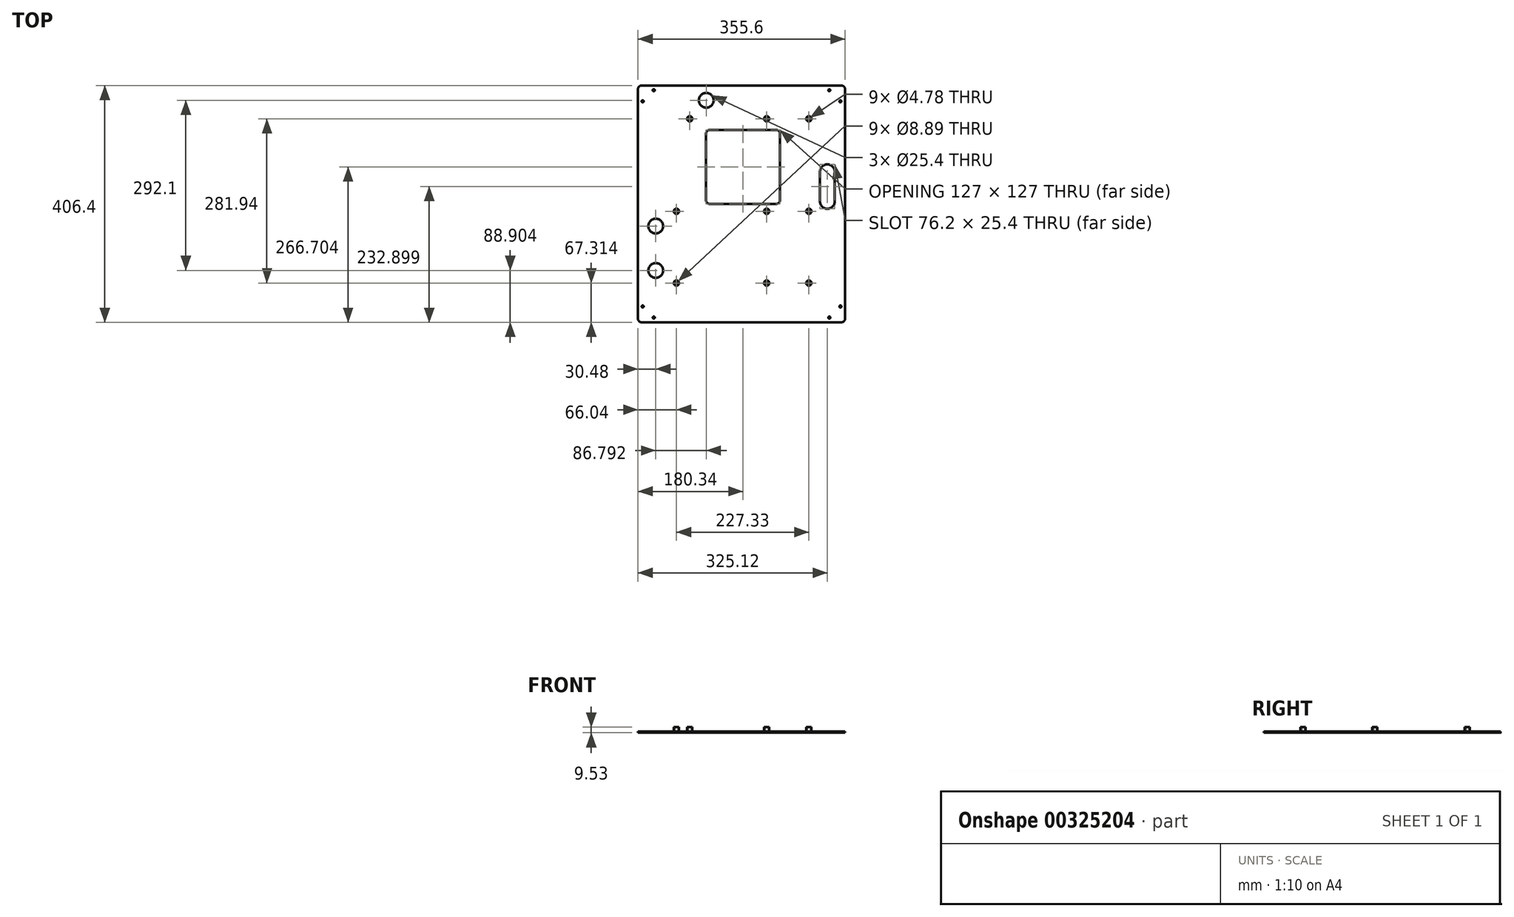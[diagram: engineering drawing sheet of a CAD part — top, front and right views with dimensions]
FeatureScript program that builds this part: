
annotation { "Feature Type Name" : "Feature", "Feature Type Description" : "" }
export const myFeature = defineFeature(function(context is Context, id is Id, definition is map)
    precondition{}
    {
        {
            var Q0;
            Q0=qCreatedBy(makeId("Top.planeOp"),FACE);
            var sketch = newSketch(context, id + "F0", { "sketchPlane" : qUnion([Q0])});
            skLineSegment(sketch, "E0.bottom", {"start": v(-150.04, 278.88) * mm, "end": v(192.86, 278.88) * mm});
            skLineSegment(sketch, "E0.top", {"start": v(-150.04, -127.52) * mm, "end": v(192.86, -127.52) * mm});
            skLineSegment(sketch, "E0.left", {"start": v(-156.4, 272.53) * mm, "end": v(-156.4, -121.17) * mm});
            skLineSegment(sketch, "E0.right", {"start": v(199.2, 272.53) * mm, "end": v(199.2, -121.17) * mm});
            skPoint(sketch, "E1", {"position": v(64.59, -76.72) * mm});
            skPoint(sketch, "E2", {"position": v(136.98, -76.72) * mm});
            skLineSegment(sketch, "E3.bottom", {"start": v(-100.51, -76.72) * mm, "end": v(143.33, -76.72) * mm});
            skLineSegment(sketch, "E3.top", {"start": v(-100.51, 228.08) * mm, "end": v(143.33, 228.08) * mm});
            skLineSegment(sketch, "E3.left", {"start": v(-100.51, -76.72) * mm, "end": v(-100.51, 228.08) * mm});
            skLineSegment(sketch, "E3.right", {"start": v(143.33, -76.72) * mm, "end": v(143.33, 228.08) * mm});
            skLineSegment(sketch, "E4", {"start": v(-100.51, 228.08) * mm, "end": v(-100.51, 140.72) * mm});
            skCircle(sketch, "E5", {"center": v(136.98, 221.73) * mm, "radius": 2.39 * mm});
            skCircle(sketch, "E6", {"center": v(64.59, 221.73) * mm, "radius": 2.39 * mm});
            skCircle(sketch, "E7", {"center": v(64.59, 221.73) * mm, "radius": 4.45 * mm});
            skCircle(sketch, "E8", {"center": v(136.98, 221.73) * mm, "radius": 4.45 * mm});
            skCircle(sketch, "E9", {"center": v(-67.5, 221.73) * mm, "radius": 2.39 * mm});
            skCircle(sketch, "E10", {"center": v(-67.5, 221.73) * mm, "radius": 4.45 * mm});
            skCircle(sketch, "E11", {"center": v(-90.35, 62.98) * mm, "radius": 2.39 * mm});
            skCircle(sketch, "E12", {"center": v(-90.35, -60.2) * mm, "radius": 2.39 * mm});
            skCircle(sketch, "E13", {"center": v(64.59, 62.98) * mm, "radius": 2.39 * mm});
            skCircle(sketch, "E14", {"center": v(64.59, -60.2) * mm, "radius": 2.39 * mm});
            skCircle(sketch, "E15", {"center": v(136.98, -60.2) * mm, "radius": 2.39 * mm});
            skCircle(sketch, "E16", {"center": v(136.98, 62.98) * mm, "radius": 2.39 * mm});
            skCircle(sketch, "E17", {"center": v(136.98, 62.98) * mm, "radius": 4.45 * mm});
            skCircle(sketch, "E18", {"center": v(64.59, 62.98) * mm, "radius": 4.45 * mm});
            skCircle(sketch, "E19", {"center": v(-90.35, 62.98) * mm, "radius": 4.45 * mm});
            skCircle(sketch, "E20", {"center": v(-90.35, -60.2) * mm, "radius": 4.45 * mm});
            skCircle(sketch, "E21", {"center": v(64.59, -60.2) * mm, "radius": 4.45 * mm});
            skCircle(sketch, "E22", {"center": v(136.98, -60.2) * mm, "radius": 4.45 * mm});
            skLineSegment(sketch, "E23", {"start": v(-100.51, -76.72) * mm, "end": v(64.59, -76.72) * mm});
            skLineSegment(sketch, "E24", {"start": v(156.03, 130.78) * mm, "end": v(156.03, 79.98) * mm});
            skLineSegment(sketch, "E25", {"start": v(181.43, 130.78) * mm, "end": v(181.43, 79.98) * mm});
            skArc(sketch, "E26", {"start": v(181.43, 130.78) * mm, "mid": v(168.73, 143.48) * mm, "end": v(156.03, 130.78) * mm});
            skArc(sketch, "E27", {"start": v(156.03, 79.98) * mm, "mid": v(168.73, 67.28) * mm, "end": v(181.43, 79.98) * mm});
            skCircle(sketch, "E28", {"center": v(-39.12, 253.48) * mm, "radius": 12.7 * mm});
            skCircle(sketch, "E29", {"center": v(-125.91, 37.58) * mm, "radius": 12.7 * mm});
            skCircle(sketch, "E30", {"center": v(-125.91, -38.62) * mm, "radius": 12.7 * mm});
            skLineSegment(sketch, "E31.bottom", {"start": v(81.1, 202.68) * mm, "end": v(-33.2, 202.68) * mm});
            skLineSegment(sketch, "E31.top", {"start": v(81.1, 75.68) * mm, "end": v(-33.2, 75.68) * mm});
            skLineSegment(sketch, "E31.left", {"start": v(87.45, 196.33) * mm, "end": v(87.45, 82.03) * mm});
            skLineSegment(sketch, "E31.right", {"start": v(-39.55, 196.33) * mm, "end": v(-39.55, 82.03) * mm});
            skPoint(sketch, "E32.visualSharp", {"position": v(87.45, 202.68) * mm});
            skArc(sketch, "E32.filletArc", {"start": v(87.45, 196.33) * mm, "mid": v(85.59, 200.82) * mm, "end": v(81.1, 202.68) * mm});
            skPoint(sketch, "E33.visualSharp", {"position": v(87.45, 75.68) * mm});
            skArc(sketch, "E33.filletArc", {"start": v(81.1, 75.68) * mm, "mid": v(85.59, 77.54) * mm, "end": v(87.45, 82.03) * mm});
            skPoint(sketch, "E34.visualSharp", {"position": v(-39.55, 75.68) * mm});
            skArc(sketch, "E34.filletArc", {"start": v(-39.55, 82.03) * mm, "mid": v(-37.7, 77.54) * mm, "end": v(-33.2, 75.68) * mm});
            skPoint(sketch, "E35.visualSharp", {"position": v(-39.55, 202.68) * mm});
            skArc(sketch, "E35.filletArc", {"start": v(-33.2, 202.68) * mm, "mid": v(-37.7, 200.82) * mm, "end": v(-39.55, 196.33) * mm});
            skPoint(sketch, "E36.visualSharp", {"position": v(-156.4, 278.88) * mm});
            skArc(sketch, "E36.filletArc", {"start": v(-150.04, 278.88) * mm, "mid": v(-154.53, 277.02) * mm, "end": v(-156.4, 272.53) * mm});
            skPoint(sketch, "E37.visualSharp", {"position": v(199.2, 278.88) * mm});
            skArc(sketch, "E37.filletArc", {"start": v(199.2, 272.53) * mm, "mid": v(197.35, 277.02) * mm, "end": v(192.86, 278.88) * mm});
            skPoint(sketch, "E38.visualSharp", {"position": v(-156.4, -127.52) * mm});
            skArc(sketch, "E38.filletArc", {"start": v(-156.4, -121.17) * mm, "mid": v(-154.53, -125.66) * mm, "end": v(-150.04, -127.52) * mm});
            skPoint(sketch, "E39.visualSharp", {"position": v(199.2, -127.52) * mm});
            skArc(sketch, "E39.filletArc", {"start": v(192.86, -127.52) * mm, "mid": v(197.35, -125.66) * mm, "end": v(199.2, -121.17) * mm});
            skCircle(sketch, "E40", {"center": v(-148.29, -100.36) * mm, "radius": 1.75 * mm});
            skCircle(sketch, "E41", {"center": v(-129.24, -119.41) * mm, "radius": 1.75 * mm});
            skCircle(sketch, "E42", {"center": v(172.06, -119.41) * mm, "radius": 1.75 * mm});
            skCircle(sketch, "E43", {"center": v(191.1, -100.36) * mm, "radius": 1.75 * mm});
            skCircle(sketch, "E44", {"center": v(-129.24, 270.78) * mm, "radius": 1.75 * mm});
            skCircle(sketch, "E45", {"center": v(-148.29, 251.73) * mm, "radius": 1.75 * mm});
            skCircle(sketch, "E46", {"center": v(172.06, 270.78) * mm, "radius": 1.75 * mm});
            skCircle(sketch, "E47", {"center": v(191.1, 251.73) * mm, "radius": 1.75 * mm});
            skSolve(sketch);
        }
        {
            var Q0;
            Q0=makeQuery(id+"F0.imprint","IMPRINT",FACE,{"disambiguationData":[TD([[makeQuery(id+"F0.imprint","IMPRINT",EDGE,{"derivedFrom":sQuery(id+"F0.wireOp",EDGE,"E3.top")}),-1.0]])]});
            var Q1;
            Q1=makeQuery(id+"F0.imprint","IMPRINT",FACE,{"disambiguationData":[TD([[makeQuery(id+"F0.imprint","IMPRINT",EDGE,{"derivedFrom":sQuery(id+"F0.wireOp",EDGE,"E13")}),1.0]])]});
            var Q2;
            {var subQ0=sQuery(id+"F0.wireOp",EDGE,"nmpgXmNF-E0IU-K8PP-zeoA-vfpKL6uIzNEA");var subQ1=makeQuery(id+"F0.imprint","IMPRINT",VERTEX,{"disambiguationData":[OD(1.0)],"derivedFrom":subQ0});Q2=makeQuery(id+"F0.imprint","IMPRINT",FACE,{"disambiguationData":[TD([[makeQuery(id+"F0.imprint","IMPRINT",EDGE,{"disambiguationData":[TD([[subQ1,1.0]])],"derivedFrom":subQ0}),-1.0]])]});}
            var Q3;
            {var subQ0=sQuery(id+"F0.wireOp",EDGE,"nmpgXmNF-E0IU-K8PP-zeoA-vfpKL6uIzNEA");var subQ1=makeQuery(id+"F0.imprint","IMPRINT",VERTEX,{"disambiguationData":[OD(1.0)],"derivedFrom":subQ0});Q3=makeQuery(id+"F0.imprint","IMPRINT",FACE,{"disambiguationData":[TD([[makeQuery(id+"F0.imprint","IMPRINT",EDGE,{"disambiguationData":[TD([[subQ1,1.0]])],"derivedFrom":subQ0}),1.0]])]});}
            var Q4;
            {var subQ0=sQuery(id+"F0.wireOp",EDGE,"nmpgXmNF-E0IU-K8PP-zeoA-vfpKL6uIzNEA");var subQ1=makeQuery(id+"F0.imprint","IMPRINT",VERTEX,{"disambiguationData":[OD(0.0)],"derivedFrom":subQ0});Q4=makeQuery(id+"F0.imprint","IMPRINT",FACE,{"disambiguationData":[TD([[makeQuery(id+"F0.imprint","IMPRINT",EDGE,{"disambiguationData":[TD([[subQ1,1.0]])],"derivedFrom":subQ0}),-1.0]])]});}
            var Q5;
            {var subQ0=sQuery(id+"F0.wireOp",EDGE,"nmpgXmNF-E0IU-K8PP-zeoA-vfpKL6uIzNEA");var subQ1=makeQuery(id+"F0.imprint","IMPRINT",VERTEX,{"disambiguationData":[OD(0.0)],"derivedFrom":subQ0});Q5=makeQuery(id+"F0.imprint","IMPRINT",FACE,{"disambiguationData":[TD([[makeQuery(id+"F0.imprint","IMPRINT",EDGE,{"disambiguationData":[TD([[subQ1,1.0]])],"derivedFrom":subQ0}),1.0]])]});}
            var Q6;
            Q6=makeQuery(id+"F0.imprint","IMPRINT",FACE,{"disambiguationData":[TD([[makeQuery(id+"F0.imprint","IMPRINT",EDGE,{"derivedFrom":sQuery(id+"F0.wireOp",EDGE,"E11")}),1.0]])]});
            var Q7;
            {var subQ7=sQuery(id+"F0.wireOp",EDGE,"E21");var subQ9=sQuery(id+"F0.wireOp",EDGE,"c2f25938-3771-4c18-96d8-fd8dbd32434b");var subQ10=makeQuery(id+"F0.imprint","INTERSECT",VERTEX,{"disambiguationData":[OD(1.0)],"derivedFrom":[subQ9,subQ7]});Q7=makeQuery(id+"F0.imprint","IMPRINT",FACE,{"disambiguationData":[TD([[makeQuery(id+"F0.imprint","IMPRINT",EDGE,{"disambiguationData":[TD([[subQ10,-1.0]])],"derivedFrom":subQ9}),-1.0]])]});}
            var Q8;
            {var subQ1=sQuery(id+"F0.wireOp",EDGE,"c2f25938-3771-4c18-96d8-fd8dbd32434b");var subQ7=sQuery(id+"F0.wireOp",EDGE,"E20");var subQ8=makeQuery(id+"F0.imprint","INTERSECT",VERTEX,{"derivedFrom":[subQ1,subQ7]});Q8=makeQuery(id+"F0.imprint","IMPRINT",FACE,{"disambiguationData":[TD([[makeQuery(id+"F0.imprint","IMPRINT",EDGE,{"disambiguationData":[TD([[subQ8,-1.0]])],"derivedFrom":subQ1}),-1.0]])]});}
            var Q9;
            {var subQ1=sQuery(id+"F0.wireOp",EDGE,"tKmp1mpe-tyhf-INWB-10SV-Ihivd2vYk6Gn.left");Q9=makeQuery(id+"F0.imprint","IMPRINT",FACE,{"disambiguationData":[TD([[makeQuery(id+"F0.imprint","IMPRINT",EDGE,{"derivedFrom":subQ1}),-1.0]])]});}
            var Q10;
            Q10=makeQuery(id+"F0.imprint","IMPRINT",FACE,{"disambiguationData":[TD([[makeQuery(id+"F0.imprint","IMPRINT",EDGE,{"derivedFrom":sQuery(id+"F0.wireOp",EDGE,"j7d80B8q-2Cgd-QsgO-YmQn-fls90DRMXYoR.bottom")}),1.0]])]});
            var Q11;
            {var subQ0=sQuery(id+"F0.wireOp",EDGE,"H0Q16ru0-qYg8-tpEI-yeED-A8eNRppSJREQ");var subQ1=sQuery(id+"F0.wireOp",EDGE,"5OOrExIu-2gan-l4Uf-qFzn-7lRf2pNMlCIK");var subQ2=makeQuery(id+"F0.imprint","INTERSECT",VERTEX,{"derivedFrom":[subQ1,subQ0]});Q11=makeQuery(id+"F0.imprint","IMPRINT",FACE,{"disambiguationData":[TD([[makeQuery(id+"F0.imprint","IMPRINT",EDGE,{"disambiguationData":[TD([[subQ2,-1.0]])],"derivedFrom":subQ1}),-1.0]])]});}
            var Q12;
            {var subQ0=sQuery(id+"F0.wireOp",EDGE,"H0Q16ru0-qYg8-tpEI-yeED-A8eNRppSJREQ");var subQ1=sQuery(id+"F0.wireOp",EDGE,"5OOrExIu-2gan-l4Uf-qFzn-7lRf2pNMlCIK");var subQ2=makeQuery(id+"F0.imprint","INTERSECT",VERTEX,{"derivedFrom":[subQ1,subQ0]});Q12=makeQuery(id+"F0.imprint","IMPRINT",FACE,{"disambiguationData":[TD([[makeQuery(id+"F0.imprint","IMPRINT",EDGE,{"disambiguationData":[TD([[subQ2,-1.0]])],"derivedFrom":subQ1}),1.0]])]});}
            var Q13;
            {var subQ0=sQuery(id+"F0.wireOp",EDGE,"f6b1ec64-6d26-4b46-bd75-5c8822b2f235");var subQ1=makeQuery(id+"F0.imprint","INTERSECT",VERTEX,{"derivedFrom":[sQuery(id+"F0.wireOp",EDGE,"c2f25938-3771-4c18-96d8-fd8dbd32434b"),subQ0]});Q13=makeQuery(id+"F0.imprint","IMPRINT",FACE,{"disambiguationData":[TD([[makeQuery(id+"F0.imprint","IMPRINT",EDGE,{"disambiguationData":[TD([[subQ1,1.0]])],"derivedFrom":subQ0}),1.0]])]});}
            var Q14;
            {var subQ0=sQuery(id+"F0.wireOp",EDGE,"f6b1ec64-6d26-4b46-bd75-5c8822b2f235");var subQ1=sQuery(id+"F0.wireOp",EDGE,"c2f25938-3771-4c18-96d8-fd8dbd32434b");var subQ2=makeQuery(id+"F0.imprint","INTERSECT",VERTEX,{"derivedFrom":[subQ1,subQ0]});Q14=makeQuery(id+"F0.imprint","IMPRINT",FACE,{"disambiguationData":[TD([[makeQuery(id+"F0.imprint","IMPRINT",EDGE,{"disambiguationData":[TD([[subQ2,1.0]])],"derivedFrom":subQ1}),1.0]])]});}
            var Q15;
            {var subQ0=sQuery(id+"F0.wireOp",EDGE,"f6b1ec64-6d26-4b46-bd75-5c8822b2f235");var subQ1=sQuery(id+"F0.wireOp",EDGE,"c2f25938-3771-4c18-96d8-fd8dbd32434b");var subQ2=makeQuery(id+"F0.imprint","INTERSECT",VERTEX,{"derivedFrom":[subQ1,subQ0]});Q15=makeQuery(id+"F0.imprint","IMPRINT",FACE,{"disambiguationData":[TD([[makeQuery(id+"F0.imprint","IMPRINT",EDGE,{"disambiguationData":[TD([[subQ2,1.0]])],"derivedFrom":subQ1}),-1.0]])]});}
            var Q16;
            {var subQ0=sQuery(id+"F0.wireOp",EDGE,"83397e81-86f9-44f2-9538-2e7c31147ec4");var subQ1=sQuery(id+"F0.wireOp",EDGE,"c2f25938-3771-4c18-96d8-fd8dbd32434b");var subQ2=makeQuery(id+"F0.imprint","INTERSECT",VERTEX,{"derivedFrom":[subQ1,subQ0]});Q16=makeQuery(id+"F0.imprint","IMPRINT",FACE,{"disambiguationData":[TD([[makeQuery(id+"F0.imprint","IMPRINT",EDGE,{"disambiguationData":[TD([[subQ2,-1.0]])],"derivedFrom":subQ1}),-1.0]])]});}
            var Q17;
            {var subQ0=sQuery(id+"F0.wireOp",EDGE,"83397e81-86f9-44f2-9538-2e7c31147ec4");var subQ1=sQuery(id+"F0.wireOp",EDGE,"c2f25938-3771-4c18-96d8-fd8dbd32434b");var subQ2=makeQuery(id+"F0.imprint","INTERSECT",VERTEX,{"derivedFrom":[subQ1,subQ0]});Q17=makeQuery(id+"F0.imprint","IMPRINT",FACE,{"disambiguationData":[TD([[makeQuery(id+"F0.imprint","IMPRINT",EDGE,{"disambiguationData":[TD([[subQ2,-1.0]])],"derivedFrom":subQ1}),1.0]])]});}
            var Q18;
            {var subQ0=sQuery(id+"F0.wireOp",EDGE,"E14");var subQ1=sQuery(id+"F0.wireOp",EDGE,"c2f25938-3771-4c18-96d8-fd8dbd32434b");var subQ2=makeQuery(id+"F0.imprint","INTERSECT",VERTEX,{"disambiguationData":[OD(0.0)],"derivedFrom":[subQ1,subQ0]});Q18=makeQuery(id+"F0.imprint","IMPRINT",FACE,{"disambiguationData":[TD([[makeQuery(id+"F0.imprint","IMPRINT",EDGE,{"disambiguationData":[TD([[subQ2,-1.0]])],"derivedFrom":subQ1}),1.0]])]});}
            var Q19;
            {var subQ0=sQuery(id+"F0.wireOp",EDGE,"E14");var subQ1=sQuery(id+"F0.wireOp",EDGE,"c2f25938-3771-4c18-96d8-fd8dbd32434b");var subQ2=makeQuery(id+"F0.imprint","INTERSECT",VERTEX,{"disambiguationData":[OD(0.0)],"derivedFrom":[subQ1,subQ0]});Q19=makeQuery(id+"F0.imprint","IMPRINT",FACE,{"disambiguationData":[TD([[makeQuery(id+"F0.imprint","IMPRINT",EDGE,{"disambiguationData":[TD([[subQ2,-1.0]])],"derivedFrom":subQ1}),-1.0]])]});}
            var Q20;
            {var subQ1=sQuery(id+"F0.wireOp",EDGE,"tKmp1mpe-tyhf-INWB-10SV-Ihivd2vYk6Gn.top");var subQ3=sQuery(id+"F0.wireOp",EDGE,"E12");var subQ4=makeQuery(id+"F0.imprint","INTERSECT",VERTEX,{"derivedFrom":[subQ1,subQ3]});Q20=makeQuery(id+"F0.imprint","IMPRINT",FACE,{"disambiguationData":[TD([[makeQuery(id+"F0.imprint","IMPRINT",EDGE,{"disambiguationData":[TD([[subQ4,1.0]])],"derivedFrom":subQ3}),1.0]])]});}
            var Q21;
            {var subQ1=sQuery(id+"F0.wireOp",EDGE,"c2f25938-3771-4c18-96d8-fd8dbd32434b");var subQ3=sQuery(id+"F0.wireOp",EDGE,"E12");var subQ4=makeQuery(id+"F0.imprint","INTERSECT",VERTEX,{"derivedFrom":[subQ1,subQ3]});Q21=makeQuery(id+"F0.imprint","IMPRINT",FACE,{"disambiguationData":[TD([[makeQuery(id+"F0.imprint","IMPRINT",EDGE,{"disambiguationData":[TD([[subQ4,-1.0]])],"derivedFrom":subQ3}),1.0]])]});}
            var Q22;
            {var subQ1=sQuery(id+"F0.wireOp",EDGE,"c2f25938-3771-4c18-96d8-fd8dbd32434b");var subQ3=sQuery(id+"F0.wireOp",EDGE,"E12");var subQ4=makeQuery(id+"F0.imprint","INTERSECT",VERTEX,{"derivedFrom":[subQ1,subQ3]});Q22=makeQuery(id+"F0.imprint","IMPRINT",FACE,{"disambiguationData":[TD([[makeQuery(id+"F0.imprint","IMPRINT",EDGE,{"disambiguationData":[TD([[subQ4,1.0]])],"derivedFrom":subQ3}),1.0]])]});}
            var Q23;
            {var subQ1=sQuery(id+"F0.wireOp",EDGE,"tKmp1mpe-tyhf-INWB-10SV-Ihivd2vYk6Gn.top");var subQ3=sQuery(id+"F0.wireOp",EDGE,"E12");var subQ4=makeQuery(id+"F0.imprint","INTERSECT",VERTEX,{"derivedFrom":[subQ1,subQ3]});Q23=makeQuery(id+"F0.imprint","IMPRINT",FACE,{"disambiguationData":[TD([[makeQuery(id+"F0.imprint","IMPRINT",EDGE,{"disambiguationData":[TD([[subQ4,-1.0]])],"derivedFrom":subQ3}),1.0]])]});}
            var Q24;
            Q24=makeQuery(id+"F0.imprint","IMPRINT",FACE,{"disambiguationData":[TD([[makeQuery(id+"F0.imprint","IMPRINT",EDGE,{"derivedFrom":sQuery(id+"F0.wireOp",EDGE,"E12")}),1.0]])]});
            var Q25;
            Q25=makeQuery(id+"F0.imprint","IMPRINT",FACE,{"disambiguationData":[TD([[makeQuery(id+"F0.imprint","IMPRINT",EDGE,{"derivedFrom":sQuery(id+"F0.wireOp",EDGE,"E14")}),1.0]])]});
            var Q26;
            Q26=makeQuery(id+"F0.imprint","IMPRINT",FACE,{"disambiguationData":[TD([[makeQuery(id+"F0.imprint","IMPRINT",EDGE,{"derivedFrom":sQuery(id+"F0.wireOp",EDGE,"E15")}),1.0]])]});
            var Q27;
            Q27=makeQuery(id+"F0.imprint","IMPRINT",FACE,{"disambiguationData":[TD([[makeQuery(id+"F0.imprint","IMPRINT",EDGE,{"derivedFrom":sQuery(id+"F0.wireOp",EDGE,"E0.bottom")}),-1.0]])]});
            extrude(context, id + "F1", {"entities" : qUnion([Q0, Q1, Q2, Q3, Q4, Q5, Q6, Q7, Q8, Q9, Q10, Q11, Q12, Q13, Q14, Q15, Q16, Q17, Q18, Q19, Q20, Q21, Q22, Q23, Q24, Q25, Q26, Q27]), "depth" : 1.9 * mm});
        }
        {
            var Q0;
            Q0=makeQuery(id+"F0.imprint","IMPRINT",FACE,{"disambiguationData":[TD([[makeQuery(id+"F0.imprint","IMPRINT",EDGE,{"derivedFrom":sQuery(id+"F0.wireOp",EDGE,"E12")}),-1.0]])]});
            var Q1;
            Q1=makeQuery(id+"F0.imprint","IMPRINT",FACE,{"disambiguationData":[TD([[makeQuery(id+"F0.imprint","IMPRINT",EDGE,{"derivedFrom":sQuery(id+"F0.wireOp",EDGE,"E11")}),-1.0]])]});
            var Q2;
            Q2=makeQuery(id+"F0.imprint","IMPRINT",FACE,{"disambiguationData":[TD([[makeQuery(id+"F0.imprint","IMPRINT",EDGE,{"derivedFrom":sQuery(id+"F0.wireOp",EDGE,"E13")}),-1.0]])]});
            var Q3;
            Q3=makeQuery(id+"F0.imprint","IMPRINT",FACE,{"disambiguationData":[TD([[makeQuery(id+"F0.imprint","IMPRINT",EDGE,{"derivedFrom":sQuery(id+"F0.wireOp",EDGE,"E16")}),-1.0]])]});
            var Q4;
            Q4=makeQuery(id+"F0.imprint","IMPRINT",FACE,{"disambiguationData":[TD([[makeQuery(id+"F0.imprint","IMPRINT",EDGE,{"derivedFrom":sQuery(id+"F0.wireOp",EDGE,"E14")}),-1.0]])]});
            var Q5;
            Q5=makeQuery(id+"F0.imprint","IMPRINT",FACE,{"disambiguationData":[TD([[makeQuery(id+"F0.imprint","IMPRINT",EDGE,{"derivedFrom":sQuery(id+"F0.wireOp",EDGE,"E15")}),-1.0]])]});
            var Q6;
            Q6=makeQuery(id+"F0.imprint","IMPRINT",FACE,{"disambiguationData":[TD([[makeQuery(id+"F0.imprint","IMPRINT",EDGE,{"derivedFrom":sQuery(id+"F0.wireOp",EDGE,"E5")}),-1.0]])]});
            var Q7;
            Q7=makeQuery(id+"F0.imprint","IMPRINT",FACE,{"disambiguationData":[TD([[makeQuery(id+"F0.imprint","IMPRINT",EDGE,{"derivedFrom":sQuery(id+"F0.wireOp",EDGE,"E6")}),-1.0]])]});
            var Q8;
            Q8=makeQuery(id+"F0.imprint","IMPRINT",FACE,{"disambiguationData":[TD([[makeQuery(id+"F0.imprint","IMPRINT",EDGE,{"derivedFrom":sQuery(id+"F0.wireOp",EDGE,"E9")}),-1.0]])]});
            extrude(context, id + "F2", {"entities" : qUnion([Q0, Q1, Q2, Q3, Q4, Q5, Q6, Q7, Q8]), "depth" : 9.52 * mm});
        }
    });
